# Revit family: 56210 PRESTO SO'O
name_source: partatom
category: Appareils sanitaires
units: mm (PartAtom-declared; Revit-internal decimal feet)

## family parameters
Basée sur le plan de construction = Non
Cote de connecteur circulaire = Utiliser le diamètre
Couper avec des vides une fois chargée = Non
Partagée = Non
Point de calcul de pièce = Non
Toujours verticalement = Oui
Type d'élément = Normal

## types (1)
- 56210 PRESTO SO'O
    Adresse = 7, RUE RACINE - 92542 MONTROUGE CEDEX FRANCE
    Arrivée d'eau = G 3/8"
    Debit = 3 l/min
    Description = Robinet mitigeur électronique pour lavabo avec alimentation 230V
    Diamètre Nominal = 12 mm  [stored 0.0393701 ft]
    Elévation par défaut = 0 mm  [stored 0 ft]
    Fabricant = LES ROBINETS PRESTO S.A.
    Famille produit = Lavabo
    Finition = Composants en métal injecté avec traitement nickel-chrome
Corps en métal moulé injecté
    Fonction = Aérateur anti-tartre haute qualité
Dispositif anti-coup de bélier
Alimentation électrique : Avec transformateur 230 Vac / 7 Vdc dans boîtier étanche IP65
Résistance thermique : Ce robinet résiste à une température de 75°C durant 30 minutes dans le cadre de chocs thermiques
Sécurité :
- Anti-brûlure : limitation de la température maximale par butée réglable
- Fermeture automatique de l'électrovanne en cas d'écoulement > à 30s, de coupure secteur ou de dégradation du détecteur

Livré avec :
- 2 Ecrous de fixation
- 1 Joint et 1 rondelle
- 2 Flexibles PEX avec écrou femelle 3/8'' (12x17) et Clapets anti-retour NF
- 2 Joints filtre
    Groupe produit = Electronique
    Hauteur = 150 mm
    LC = 15 mm  [stored 0.0492126 ft]
    Lien CCTP = http://www.prestodatashare.com
    Lien fiche produit = http://www.prestodatashare.com
    Lien notice d'utilisation = http://www.prestodatashare.com
    Longueur = 155 mm
    Materiau principal = Laiton
    Materiau secondaire = Chrome
    Modèle = 56210 PRESTO SO'O
    Nom du fabricant = Presto
    PC = 30 mm  [stored 0.0984252 ft]
    Pays designer = France
    Pays fabricant = France
    Perte de charge = 0.0 Pa
    Poids Net (Kg) = 0
    Pression = 1 à 5 bars
    Product SKU = 56210
    Profondeur = 58 mm
    Raccordement = G 3/8'' (12x17)
    Reference = 56214
    UNSPSC Code = 301815
    URL = http://www.prestodatashare.com
    Variantes = 56214

note: [stored X ft] marks values corroborated as IEEE doubles in the binary element streams (Revit-internal decimal feet)

## geometry (parser evidence)
native form markers: Blend x1
no freeform markers — native parametric forms only
